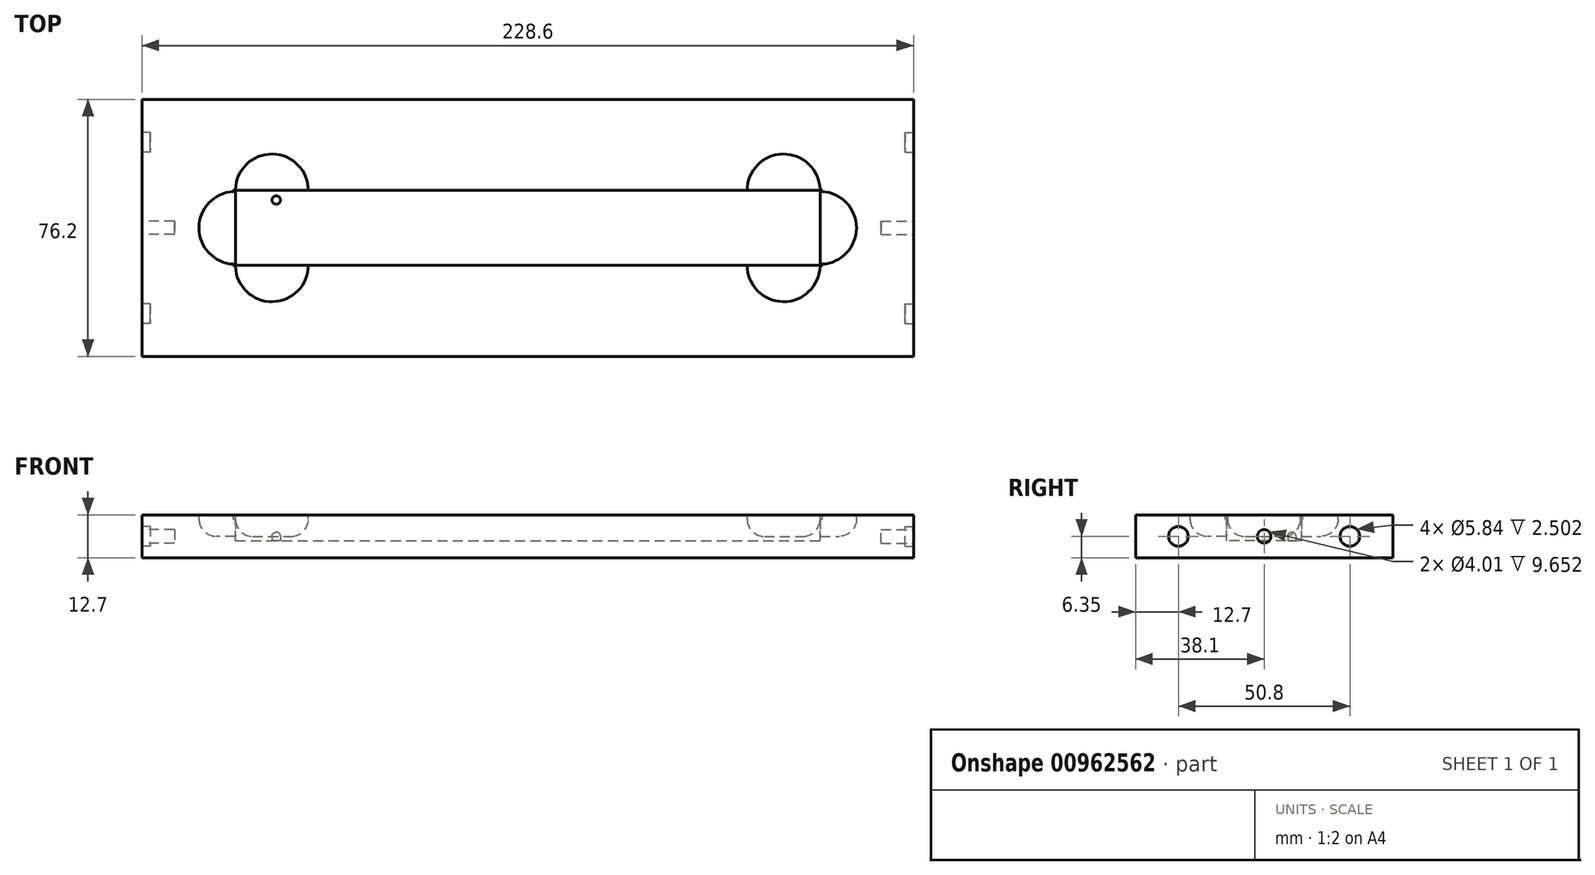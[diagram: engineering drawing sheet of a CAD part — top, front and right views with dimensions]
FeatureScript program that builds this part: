
annotation { "Feature Type Name" : "Feature", "Feature Type Description" : "" }
export const myFeature = defineFeature(function(context is Context, id is Id, definition is map)
    precondition{}
    {
        {
            var Q0;
            Q0=qCreatedBy(makeId("Top.planeOp"),FACE);
            var sketch = newSketch(context, id + "F0", { "sketchPlane" : qUnion([Q0])});
            skLineSegment(sketch, "E0.bottom", {"start": v(-114.3, 38.1) * mm, "end": v(114.3, 38.1) * mm});
            skLineSegment(sketch, "E0.top", {"start": v(-114.3, -38.1) * mm, "end": v(114.3, -38.1) * mm});
            skLineSegment(sketch, "E0.left", {"start": v(-114.3, 38.1) * mm, "end": v(-114.3, -38.1) * mm});
            skLineSegment(sketch, "E0.right", {"start": v(114.3, 38.1) * mm, "end": v(114.3, -38.1) * mm});
            skPoint(sketch, "E0.middle", {"position": v(0, 0) * mm});
            skSolve(sketch);
        }
        {
            var Q0;
            Q0 = qSketchRegion(id + "F0", true);
            extrude(context, id + "F1", {"entities" : qUnion([Q0]), "depth" : 12.7 * mm, "offsetDistance" : 25.4 * mm});
        }
        {
            var Q0;
            Q0=makeQuery(id+"F1.opExtrude","CAP_FACE",FACE,{"disambiguationData":[OSD([sQuery(id+"F0.wireOp",EDGE,"E0.bottom"),sQuery(id+"F0.wireOp",EDGE,"E0.top"),sQuery(id+"F0.wireOp",EDGE,"E0.left"),sQuery(id+"F0.wireOp",EDGE,"E0.right")])],"isStart":false});
            var sketch = newSketch(context, id + "F2", { "sketchPlane" : qUnion([Q0])});
            skLineSegment(sketch, "E1.bottom", {"start": v(-86.6, 11.1) * mm, "end": v(86.6, 11.1) * mm});
            skLineSegment(sketch, "E1.top", {"start": v(-86.6, -11.1) * mm, "end": v(86.6, -11.1) * mm});
            skLineSegment(sketch, "E1.left", {"start": v(-86.6, 11.1) * mm, "end": v(-86.6, -11.1) * mm});
            skLineSegment(sketch, "E1.right", {"start": v(86.6, 11.1) * mm, "end": v(86.6, -11.1) * mm});
            skPoint(sketch, "E1.middle", {"position": v(0, 0) * mm});
            skSolve(sketch);
        }
        {
            var Q0;
            Q0=makeQuery(id+"F2.imprint","IMPRINT",FACE,{"disambiguationData":[TD([[makeQuery(id+"F2.imprint","IMPRINT",EDGE,{"derivedFrom":sQuery(id+"F2.wireOp",EDGE,"E1.bottom")}),-1.0]])]});
            extrude(context, id + "F3", {"entities" : qUnion([Q0]), "operationType" : NewBodyOperationType.REMOVE, "oppositeDirection" : true, "depth" : 7.62 * mm, "offsetDistance" : 25.4 * mm});
        }
        {
            var Q0;
            Q0=makeQuery(id+"F1.opExtrude","CAP_FACE",FACE,{"disambiguationData":[OSD([sQuery(id+"F0.wireOp",EDGE,"E0.bottom"),sQuery(id+"F0.wireOp",EDGE,"E0.top"),sQuery(id+"F0.wireOp",EDGE,"E0.left"),sQuery(id+"F0.wireOp",EDGE,"E0.right")])],"isStart":false});
            var sketch = newSketch(context, id + "F4", { "sketchPlane" : qUnion([Q0])});
            skCircle(sketch, "E2", {"center": v(-86.6, 0) * mm, "radius": 10.8 * mm});
            skCircle(sketch, "E3", {"center": v(86.6, 0) * mm, "radius": 10.8 * mm});
            skSolve(sketch);
        }
        {
            var Q0;
            Q0 = qSketchRegion(id + "F4", true);
            extrude(context, id + "F5", {"entities" : qUnion([Q0]), "operationType" : NewBodyOperationType.REMOVE, "oppositeDirection" : true, "depth" : 6.35 * mm, "offsetDistance" : 25.4 * mm});
        }
        {
            var Q0;
            Q0=makeQuery(id+"F1.opExtrude","CAP_FACE",FACE,{"disambiguationData":[OSD([sQuery(id+"F0.wireOp",EDGE,"E0.bottom"),sQuery(id+"F0.wireOp",EDGE,"E0.top"),sQuery(id+"F0.wireOp",EDGE,"E0.left"),sQuery(id+"F0.wireOp",EDGE,"E0.right")])],"isStart":false});
            var sketch = newSketch(context, id + "F6", { "sketchPlane" : qUnion([Q0])});
            skLineSegment(sketch, "E4", {"start": v(-86.6, 11.1) * mm, "end": v(-75.8, 11.1) * mm});
            skLineSegment(sketch, "E5", {"start": v(-86.6, -11.1) * mm, "end": v(-75.8, -11.1) * mm});
            skLineSegment(sketch, "E6", {"start": v(86.6, 11.1) * mm, "end": v(75.8, 11.1) * mm});
            skLineSegment(sketch, "E7", {"start": v(86.6, -11.1) * mm, "end": v(75.8, -11.1) * mm});
            skCircle(sketch, "E8", {"center": v(-75.8, 11.1) * mm, "radius": 10.8 * mm});
            skCircle(sketch, "E9", {"center": v(-75.8, -11.1) * mm, "radius": 10.8 * mm});
            skCircle(sketch, "E10", {"center": v(75.8, -11.1) * mm, "radius": 10.8 * mm});
            skCircle(sketch, "E11", {"center": v(75.8, 11.1) * mm, "radius": 10.8 * mm});
            skSolve(sketch);
        }
        {
            var Q0;
            {var subQ0=sQuery(id+"F6.wireOp",EDGE,"E5");Q0=makeQuery(id+"F6.imprint","IMPRINT",FACE,{"disambiguationData":[TD([[makeQuery(id+"F6.imprint","IMPRINT",EDGE,{"derivedFrom":subQ0}),-1.0]])]});}
            var Q1;
            {var subQ0=sQuery(id+"F6.wireOp",EDGE,"E6");Q1=makeQuery(id+"F6.imprint","IMPRINT",FACE,{"disambiguationData":[TD([[makeQuery(id+"F6.imprint","IMPRINT",EDGE,{"derivedFrom":subQ0}),1.0]])]});}
            var Q2;
            {var subQ0=sQuery(id+"F6.wireOp",EDGE,"E7");Q2=makeQuery(id+"F6.imprint","IMPRINT",FACE,{"disambiguationData":[TD([[makeQuery(id+"F6.imprint","IMPRINT",EDGE,{"derivedFrom":subQ0}),-1.0]])]});}
            var Q3;
            {var subQ0=sQuery(id+"F6.wireOp",EDGE,"E4");Q3=makeQuery(id+"F6.imprint","IMPRINT",FACE,{"disambiguationData":[TD([[makeQuery(id+"F6.imprint","IMPRINT",EDGE,{"derivedFrom":subQ0}),1.0]])]});}
            extrude(context, id + "F7", {"entities" : qUnion([Q0, Q1, Q2, Q3]), "operationType" : NewBodyOperationType.REMOVE, "oppositeDirection" : true, "depth" : 6.35 * mm, "offsetDistance" : 25.4 * mm});
        }
        {
            var Q0;
            Q0=makeQuery(id+"F1.opExtrude","SWEPT_FACE",FACE,{"disambiguationData":[OSD([sQuery(id+"F0.wireOp",EDGE,"E0.left")])]});
            var sketch = newSketch(context, id + "F8", { "sketchPlane" : qUnion([Q0])});
            skCircle(sketch, "E12", {"center": v(0, 6.35) * mm, "radius": 2 * mm});
            skSolve(sketch);
        }
        {
            var Q0;
            Q0 = qSketchRegion(id + "F8", true);
            extrude(context, id + "F9", {"entities" : qUnion([Q0]), "operationType" : NewBodyOperationType.REMOVE, "oppositeDirection" : true, "depth" : 9.65 * mm, "offsetDistance" : 25.4 * mm});
        }
        {
            var Q0;
            Q0=makeQuery(id+"F1.opExtrude","SWEPT_FACE",FACE,{"disambiguationData":[OSD([sQuery(id+"F0.wireOp",EDGE,"E0.right")])]});
            var sketch = newSketch(context, id + "F10", { "sketchPlane" : qUnion([Q0])});
            skCircle(sketch, "E13", {"center": v(0, 6.35) * mm, "radius": 2 * mm});
            skSolve(sketch);
        }
        {
            var Q0;
            Q0 = qSketchRegion(id + "F10", true);
            extrude(context, id + "F11", {"entities" : qUnion([Q0]), "operationType" : NewBodyOperationType.REMOVE, "oppositeDirection" : true, "depth" : 9.65 * mm, "offsetDistance" : 25.4 * mm});
        }
        {
            var Q0;
            Q0=makeQuery(id+"F1.opExtrude","SWEPT_FACE",FACE,{"disambiguationData":[OSD([sQuery(id+"F0.wireOp",EDGE,"E0.left")])]});
            var sketch = newSketch(context, id + "F12", { "sketchPlane" : qUnion([Q0])});
            skLineSegment(sketch, "E14.bottom", {"start": v(-38.1, 12.7) * mm, "end": v(38.1, 12.7) * mm});
            skLineSegment(sketch, "E14.top", {"start": v(-38.1, 0) * mm, "end": v(38.1, 0) * mm});
            skLineSegment(sketch, "E14.left", {"start": v(-38.1, 12.7) * mm, "end": v(-38.1, 0) * mm});
            skLineSegment(sketch, "E14.right", {"start": v(38.1, 12.7) * mm, "end": v(38.1, 0) * mm});
            skPoint(sketch, "E14.middle", {"position": v(0, 6.35) * mm});
            skCircle(sketch, "E15", {"center": v(-25.4, 6.35) * mm, "radius": 2.92 * mm});
            skCircle(sketch, "E16", {"center": v(25.4, 6.35) * mm, "radius": 2.92 * mm});
            skSolve(sketch);
        }
        {
            var Q0;
            Q0=makeQuery(id+"F12.imprint","IMPRINT",FACE,{"disambiguationData":[TD([[makeQuery(id+"F12.imprint","IMPRINT",EDGE,{"derivedFrom":sQuery(id+"F12.wireOp",EDGE,"E15")}),1.0]])]});
            var Q1;
            Q1=makeQuery(id+"F12.imprint","IMPRINT",FACE,{"disambiguationData":[TD([[makeQuery(id+"F12.imprint","IMPRINT",EDGE,{"derivedFrom":sQuery(id+"F12.wireOp",EDGE,"E16")}),1.0]])]});
            extrude(context, id + "F13", {"entities" : qUnion([Q0, Q1]), "operationType" : NewBodyOperationType.REMOVE, "oppositeDirection" : true, "depth" : 2.5 * mm, "offsetDistance" : 25.4 * mm});
        }
        {
            var Q0;
            Q0=makeQuery(id+"F1.opExtrude","SWEPT_FACE",FACE,{"disambiguationData":[OSD([sQuery(id+"F0.wireOp",EDGE,"E0.right")])]});
            var sketch = newSketch(context, id + "F14", { "sketchPlane" : qUnion([Q0])});
            skLineSegment(sketch, "E17.bottom", {"start": v(-38.1, 12.7) * mm, "end": v(38.1, 12.7) * mm});
            skLineSegment(sketch, "E17.top", {"start": v(-38.1, 0) * mm, "end": v(38.1, 0) * mm});
            skLineSegment(sketch, "E17.left", {"start": v(-38.1, 12.7) * mm, "end": v(-38.1, 0) * mm});
            skLineSegment(sketch, "E17.right", {"start": v(38.1, 12.7) * mm, "end": v(38.1, 0) * mm});
            skPoint(sketch, "E17.middle", {"position": v(0, 6.35) * mm});
            skCircle(sketch, "E18", {"center": v(-25.4, 6.35) * mm, "radius": 2.92 * mm});
            skCircle(sketch, "E19", {"center": v(25.4, 6.35) * mm, "radius": 2.92 * mm});
            skSolve(sketch);
        }
        {
            var Q0;
            Q0=makeQuery(id+"F14.imprint","IMPRINT",FACE,{"disambiguationData":[TD([[makeQuery(id+"F14.imprint","IMPRINT",EDGE,{"derivedFrom":sQuery(id+"F14.wireOp",EDGE,"E18")}),1.0]])]});
            var Q1;
            Q1=makeQuery(id+"F14.imprint","IMPRINT",FACE,{"disambiguationData":[TD([[makeQuery(id+"F14.imprint","IMPRINT",EDGE,{"derivedFrom":sQuery(id+"F14.wireOp",EDGE,"E19")}),1.0]])]});
            extrude(context, id + "F15", {"entities" : qUnion([Q0, Q1]), "operationType" : NewBodyOperationType.REMOVE, "oppositeDirection" : true, "depth" : 2.5 * mm, "offsetDistance" : 25.4 * mm});
        }
        {
            var Q0;
            Q0=makeQuery(id+"F5.boolean.opBoolean","COPY",EDGE,{"derivedFrom":makeQuery(id+"F5.opExtrude","CAP_EDGE",EDGE,{"disambiguationData":[OSD([sQuery(id+"F4.wireOp",EDGE,"E2")])],"isStart":false})});
            var Q1;
            Q1=makeQuery(id+"F7.boolean.opBoolean","COPY",EDGE,{"derivedFrom":makeQuery(id+"F7.opExtrude","CAP_EDGE",EDGE,{"disambiguationData":[OSD([sQuery(id+"F6.wireOp",EDGE,"E8")])],"isStart":false})});
            var Q2;
            Q2=makeQuery(id+"F7.boolean.opBoolean","COPY",EDGE,{"derivedFrom":makeQuery(id+"F7.opExtrude","CAP_EDGE",EDGE,{"disambiguationData":[OSD([sQuery(id+"F6.wireOp",EDGE,"E9")])],"isStart":false})});
            var Q3;
            Q3=makeQuery(id+"F7.boolean.opBoolean","COPY",EDGE,{"derivedFrom":makeQuery(id+"F7.opExtrude","CAP_EDGE",EDGE,{"disambiguationData":[OSD([sQuery(id+"F6.wireOp",EDGE,"E11")])],"isStart":false})});
            var Q4;
            Q4=makeQuery(id+"F5.boolean.opBoolean","COPY",EDGE,{"derivedFrom":makeQuery(id+"F5.opExtrude","CAP_EDGE",EDGE,{"disambiguationData":[OSD([sQuery(id+"F4.wireOp",EDGE,"E3")])],"isStart":false})});
            var Q5;
            Q5=makeQuery(id+"F7.boolean.opBoolean","COPY",EDGE,{"derivedFrom":makeQuery(id+"F7.opExtrude","CAP_EDGE",EDGE,{"disambiguationData":[OSD([sQuery(id+"F6.wireOp",EDGE,"E10")])],"isStart":false})});
            fillet(context, id + "F16", {"entities" : qUnion([Q0, Q1, Q2, Q3, Q4, Q5]), "radius" : 5.08 * mm, "tangentPropagation" : true, "allowEdgeOverflow" : false});
        }
        {
            var Q0;
            Q0=makeQuery(id+"F3.boolean.opBoolean","COPY",FACE,{"derivedFrom":makeQuery(id+"F3.opExtrude","CAP_FACE",FACE,{"disambiguationData":[OSD([sQuery(id+"F2.wireOp",EDGE,"E1.bottom"),sQuery(id+"F2.wireOp",EDGE,"E1.top"),sQuery(id+"F2.wireOp",EDGE,"E1.left"),sQuery(id+"F2.wireOp",EDGE,"E1.right")])],"isStart":false})});
            var sketch = newSketch(context, id + "F17", { "sketchPlane" : qUnion([Q0])});
            skLineSegment(sketch, "E20.bottom", {"start": v(0, 11.1) * mm, "end": v(-74.5, 11.1) * mm});
            skLineSegment(sketch, "E20.top", {"start": v(0, 8.25) * mm, "end": v(-74.5, 8.25) * mm});
            skLineSegment(sketch, "E20.left", {"start": v(0, 11.1) * mm, "end": v(0, 8.25) * mm});
            skLineSegment(sketch, "E20.right", {"start": v(-74.5, 11.1) * mm, "end": v(-74.5, 8.25) * mm});
            skCircle(sketch, "E21", {"center": v(-74.5, 8.25) * mm, "radius": 1.25 * mm});
            skSolve(sketch);
        }
        {
            var Q0;
            {var subQ0=sQuery(id+"F17.wireOp",EDGE,"E20.right");var subQ1=sQuery(id+"F17.wireOp",EDGE,"E20.top");var subQ2=makeQuery(id+"F17.imprint","INTERSECT",VERTEX,{"derivedFrom":[subQ1,subQ0]});Q0=makeQuery(id+"F17.imprint","IMPRINT",FACE,{"disambiguationData":[TD([[makeQuery(id+"F17.imprint","IMPRINT",EDGE,{"disambiguationData":[TD([[subQ2,1.0]])],"derivedFrom":subQ1}),1.0]])]});}
            var Q1;
            {var subQ0=sQuery(id+"F17.wireOp",EDGE,"E20.right");var subQ1=sQuery(id+"F17.wireOp",EDGE,"E20.top");var subQ2=makeQuery(id+"F17.imprint","INTERSECT",VERTEX,{"derivedFrom":[subQ1,subQ0]});Q1=makeQuery(id+"F17.imprint","IMPRINT",FACE,{"disambiguationData":[TD([[makeQuery(id+"F17.imprint","IMPRINT",EDGE,{"disambiguationData":[TD([[subQ2,1.0]])],"derivedFrom":subQ1}),-1.0]])]});}
            extrude(context, id + "F18", {"entities" : qUnion([Q0, Q1]), "operationType" : NewBodyOperationType.ADD, "depth" : 2.5 * mm, "offsetDistance" : 25.4 * mm});
        }
        {
            var Q0;
            Q0=makeQuery(id+"F18.opExtrude","CAP_EDGE",EDGE,{"disambiguationData":[OSD([sQuery(id+"F17.wireOp",EDGE,"E21")])],"isStart":false});
            fillet(context, id + "F19", {"entities" : qUnion([Q0]), "radius" : 1.24 * mm, "tangentPropagation" : true, "allowEdgeOverflow" : false});
        }
        {
            var Q0;
            Q0=makeQuery(id+"F1.opExtrude","CAP_FACE",FACE,{"disambiguationData":[OSD([sQuery(id+"F0.wireOp",EDGE,"E0.bottom"),sQuery(id+"F0.wireOp",EDGE,"E0.top"),sQuery(id+"F0.wireOp",EDGE,"E0.left"),sQuery(id+"F0.wireOp",EDGE,"E0.right")])],"isStart":false});
            var sketch = newSketch(context, id + "F20", { "sketchPlane" : qUnion([Q0])});
            skCircle(sketch, "E22", {"center": v(-86.6, 10.8) * mm, "radius": 0.64 * mm});
            skCircle(sketch, "E23", {"center": v(-86.6, -10.8) * mm, "radius": 0.64 * mm});
            skCircle(sketch, "E24", {"center": v(86.6, 10.8) * mm, "radius": 0.64 * mm});
            skCircle(sketch, "E25", {"center": v(86.6, -10.8) * mm, "radius": 0.64 * mm});
            skSolve(sketch);
        }
        {
            var Q0;
            {var subQ0=sQuery(id+"F20.wireOp",EDGE,"E22");var subQ1=sQuery(id+"F4.wireOp",EDGE,"E2");var subQ2=makeQuery(id+"F5.boolean.opBoolean","COPY",EDGE,{"derivedFrom":makeQuery(id+"F5.opExtrude","CAP_EDGE",EDGE,{"disambiguationData":[OSD([subQ1])],"isStart":true})});var subQ3=makeQuery(id+"F20.imprint","INTERSECT",VERTEX,{"derivedFrom":[subQ2,subQ0]});Q0=makeQuery(id+"F20.imprint","IMPRINT",FACE,{"disambiguationData":[TD([[makeQuery(id+"F20.imprint","IMPRINT",EDGE,{"disambiguationData":[TD([[subQ3,1.0]])],"derivedFrom":subQ0}),1.0]])]});}
            var Q1;
            {var subQ0=sQuery(id+"F20.wireOp",EDGE,"E23");var subQ1=sQuery(id+"F4.wireOp",EDGE,"E2");var subQ2=makeQuery(id+"F5.boolean.opBoolean","COPY",EDGE,{"derivedFrom":makeQuery(id+"F5.opExtrude","CAP_EDGE",EDGE,{"disambiguationData":[OSD([subQ1])],"isStart":true})});var subQ3=makeQuery(id+"F20.imprint","INTERSECT",VERTEX,{"derivedFrom":[subQ2,subQ0]});Q1=makeQuery(id+"F20.imprint","IMPRINT",FACE,{"disambiguationData":[TD([[makeQuery(id+"F20.imprint","IMPRINT",EDGE,{"disambiguationData":[TD([[subQ3,-1.0]])],"derivedFrom":subQ0}),1.0]])]});}
            var Q2;
            {var subQ0=sQuery(id+"F20.wireOp",EDGE,"E24");var subQ1=sQuery(id+"F4.wireOp",EDGE,"E3");var subQ2=makeQuery(id+"F5.boolean.opBoolean","COPY",EDGE,{"derivedFrom":makeQuery(id+"F5.opExtrude","CAP_EDGE",EDGE,{"disambiguationData":[OSD([subQ1])],"isStart":true})});var subQ3=makeQuery(id+"F20.imprint","INTERSECT",VERTEX,{"derivedFrom":[subQ2,subQ0]});Q2=makeQuery(id+"F20.imprint","IMPRINT",FACE,{"disambiguationData":[TD([[makeQuery(id+"F20.imprint","IMPRINT",EDGE,{"disambiguationData":[TD([[subQ3,-1.0]])],"derivedFrom":subQ0}),1.0]])]});}
            var Q3;
            {var subQ0=sQuery(id+"F20.wireOp",EDGE,"E25");var subQ1=sQuery(id+"F4.wireOp",EDGE,"E3");var subQ2=makeQuery(id+"F5.boolean.opBoolean","COPY",EDGE,{"derivedFrom":makeQuery(id+"F5.opExtrude","CAP_EDGE",EDGE,{"disambiguationData":[OSD([subQ1])],"isStart":true})});var subQ3=makeQuery(id+"F20.imprint","INTERSECT",VERTEX,{"derivedFrom":[subQ2,subQ0]});Q3=makeQuery(id+"F20.imprint","IMPRINT",FACE,{"disambiguationData":[TD([[makeQuery(id+"F20.imprint","IMPRINT",EDGE,{"disambiguationData":[TD([[subQ3,1.0]])],"derivedFrom":subQ0}),1.0]])]});}
            extrude(context, id + "F21", {"entities" : qUnion([Q0, Q1, Q2, Q3]), "operationType" : NewBodyOperationType.REMOVE, "oppositeDirection" : true, "depth" : 1.27 * mm, "offsetDistance" : 25.4 * mm});
        }
    });
